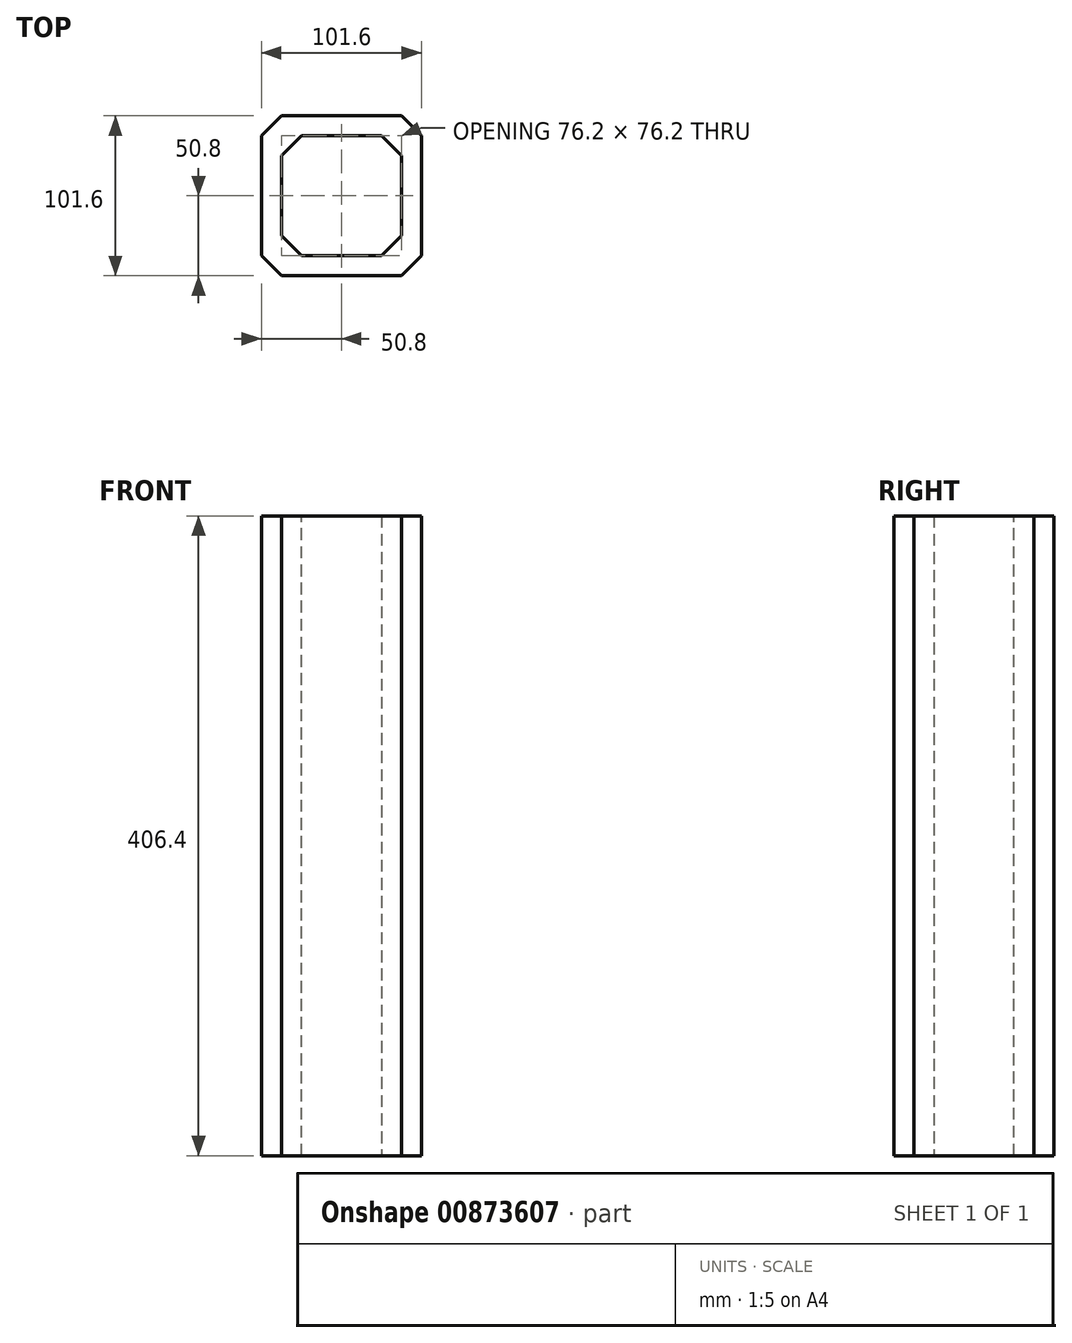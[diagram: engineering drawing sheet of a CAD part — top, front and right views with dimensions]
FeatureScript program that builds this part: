
annotation { "Feature Type Name" : "Feature", "Feature Type Description" : "" }
export const myFeature = defineFeature(function(context is Context, id is Id, definition is map)
    precondition{}
    {
        {
            var Q0;
            Q0=qCreatedBy(makeId("Top.planeOp"),FACE);
            var sketch = newSketch(context, id + "F0", { "sketchPlane" : qUnion([Q0])});
            skLineSegment(sketch, "E0.bottom", {"start": v(0, 0) * mm, "end": v(101.6, 0) * mm});
            skLineSegment(sketch, "E0.top", {"start": v(0, 101.6) * mm, "end": v(101.6, 101.6) * mm});
            skLineSegment(sketch, "E0.left", {"start": v(0, 0) * mm, "end": v(0, 101.6) * mm});
            skLineSegment(sketch, "E0.right", {"start": v(101.6, 0) * mm, "end": v(101.6, 101.6) * mm});
            skLineSegment(sketch, "E1.0", {"start": v(12.7, 12.7) * mm, "end": v(12.7, 88.9) * mm});
            skLineSegment(sketch, "E1.1", {"start": v(12.7, 12.7) * mm, "end": v(88.9, 12.7) * mm});
            skLineSegment(sketch, "E1.2", {"start": v(88.9, 12.7) * mm, "end": v(88.9, 88.9) * mm});
            skLineSegment(sketch, "E1.3", {"start": v(12.7, 88.9) * mm, "end": v(88.9, 88.9) * mm});
            skSolve(sketch);
        }
        {
            var Q0;
            Q0=qSketchRegion(id+"F0",true);
            extrude(context, id + "F1", {"entities" : qUnion([Q0]), "depth" : 406.4 * mm, "offsetDistance" : 25.4 * mm});
        }
        {
            var Q0;
            Q0=makeQuery(id+"F1.opExtrude","SWEPT_EDGE",EDGE,{"disambiguationData":[OSD([sQuery(id+"F0.wireOp",EDGE,"E1.0"),sQuery(id+"F0.wireOp",EDGE,"E1.3")])]});
            var Q1;
            Q1=makeQuery(id+"F1.opExtrude","SWEPT_EDGE",EDGE,{"disambiguationData":[OSD([sQuery(id+"F0.wireOp",EDGE,"E1.2"),sQuery(id+"F0.wireOp",EDGE,"E1.3")])]});
            var Q2;
            Q2=makeQuery(id+"F1.opExtrude","SWEPT_EDGE",EDGE,{"disambiguationData":[OSD([sQuery(id+"F0.wireOp",EDGE,"E1.1"),sQuery(id+"F0.wireOp",EDGE,"E1.2")])]});
            var Q3;
            Q3=makeQuery(id+"F1.opExtrude","SWEPT_EDGE",EDGE,{"disambiguationData":[OSD([sQuery(id+"F0.wireOp",EDGE,"E1.0"),sQuery(id+"F0.wireOp",EDGE,"E1.1")])]});
            chamfer(context, id + "F2", {"entities" : qUnion([Q0, Q1, Q2, Q3]), "width" : 12.7 * mm, "tangentPropagation" : true});
        }
        {
            var Q0;
            Q0=makeQuery(id+"F1.opExtrude","SWEPT_EDGE",EDGE,{"disambiguationData":[OSD([sQuery(id+"F0.wireOp",EDGE,"E0.bottom"),sQuery(id+"F0.wireOp",EDGE,"E0.right")])]});
            var Q1;
            Q1=makeQuery(id+"F1.opExtrude","SWEPT_EDGE",EDGE,{"disambiguationData":[OSD([sQuery(id+"F0.wireOp",EDGE,"E0.top"),sQuery(id+"F0.wireOp",EDGE,"E0.right")])]});
            var Q2;
            Q2=makeQuery(id+"F1.opExtrude","SWEPT_EDGE",EDGE,{"disambiguationData":[OSD([sQuery(id+"F0.wireOp",EDGE,"E0.bottom"),sQuery(id+"F0.wireOp",EDGE,"E0.left")])]});
            var Q3;
            Q3=makeQuery(id+"F1.opExtrude","SWEPT_EDGE",EDGE,{"disambiguationData":[OSD([sQuery(id+"F0.wireOp",EDGE,"E0.top"),sQuery(id+"F0.wireOp",EDGE,"E0.left")])]});
            chamfer(context, id + "F3", {"entities" : qUnion([Q0, Q1, Q2, Q3]), "width" : 12.7 * mm, "tangentPropagation" : true});
        }
    });
